# Revit family: 3_天吊埋込タイプ 排気消音タイプ 単相100V_3相200V-60
name_source: partatom
category: 機械設備
units: mm (PartAtom-declared; Revit-internal decimal feet)

## family parameters
OmniClass タイトル = Centrifugal Fans
OmniClass 番号 = 23.75.35.17.27
パーツ タイプ = 割り込み
ロード時にボイドで切り取り = いいえ
丸型コネクタ寸法 = 直径を使用
作業面ベース = いいえ
共有 = いいえ
常に垂直 = はい
部屋計算ポイント = はい

## types (6) — shared parameters
Clearance Left = 450  [stored 1.47638 ft]
Height = 350  [stored 1.14829 ft]
IfcExportAs = IfcFanType
IfcExportType = CENTRIFUGALFORWARDCURVED
MID静圧 = 0.0 Pa
MID風量 = 0.0 m³/h
OmniClassCode = 23-33 31 19 13 15
URL = https://www.mitsubishielectric.co.jp
Uniclass2015Code = Pr_65_67_29_12
Uniclass2015Title = Centrifugal fans
Uniclass2015Version = Systems v1.9
サービススペース = はい
ファンの種類 = 多翼形
仕様書バージョン = Version1.0
企業コード = 108420
分類コード = 50052502100020
周波数 = 60 Hz
呼称 = 消音ボックス付送風機
実風量 = 0.0 m³/h
本体マテリアル = 溶融亜鉛めっき鋼板
極 = 4
法定耐用年数 = 15
番手 = ♯1 1/2
盤工事区分 = 電気工事
積算_科目 = 2 換気設備
製品リリース年月 = 2008年12月1日
製品出荷対象 = 国内
製造元 = 三菱電機株式会社
設置方法 = 天吊
説明 = ストレートシロッコファン天吊埋込タイプ（消音形排気消音タイプ）
負荷分類 = 3_ファン類
運転質量 = 0.00 kg
zero-valued in all types: Clearance Back, Clearance Bottom, Clearance Front, Clearance Right, Clearance Top

## per-type parameters (varying)
| type | Depth | M | MAX静圧 | MAX風量 | MIN静圧 | MIN風量 | Width | ダクト径 | 価格 | 天吊金具ピッチ奥行 | 天吊金具ピッチ幅 | 形名 | 極数 | 消費電力 | 相 | 製品質量 | 質量 | 電動機出力 | 電圧 | 騒音レベル(dB(A)) | 騒音レベル(dB(A))_側面 | 騒音レベル(dB(A))_吐出 | 騒音レベル(dB(A))_吸込 |
| BFS-120SHU | 887  [stored 2.9101 ft] | 85  [stored 0.278871 ft] | 265.0 Pa | 1200.0 m³/h | 179.0 Pa | 989.0 m³/h | 455  [stored 1.49278 ft] | 250 mm | 179000 $ | 851  [stored 2.79199 ft] | 550  [stored 1.80446 ft] | BFS-SHU : BFS-120SHU | 2 | 330 W | 1 | 28.00 kg | 33.60 kg | 270 W | 100 V | 47 | 35 | 47 | 41.5 |
| BFS-150SHU | 1041 | 85  [stored 0.278871 ft] | 294.0 Pa | 1500.0 m³/h | 179.0 Pa | 1164.0 m³/h | 455  [stored 1.49278 ft] | 250 mm | 186000 $ | 1005  [stored 3.29724 ft] | 550  [stored 1.80446 ft] | BFS-SHU : BFS-150SHU | 2 | 480 W | 1 | 30.00 kg | 36.00 kg | 300 W | 100 V | 50 | 37 | 50 | 42.5 |
| BFS-120THU | 887  [stored 2.9101 ft] | 85  [stored 0.278871 ft] | 265.0 Pa | 1200.0 m³/h | 119.0 Pa | 789.0 m³/h | 455  [stored 1.49278 ft] | 250 mm | 179000 $ | 851  [stored 2.79199 ft] | 550  [stored 1.80446 ft] | BFS-THU : BFS-120THU | 3 | 330 W | 3 | 28.00 kg | 33.60 kg | 240 W | 200 V | 47 | 35 | 47 | 41.5 |
| BFS-150THU | 1041 | 85  [stored 0.278871 ft] | 294.0 Pa | 1500.0 m³/h | 129.0 Pa | 995.0 m³/h | 455  [stored 1.49278 ft] | 250 mm | 186000 $ | 1005  [stored 3.29724 ft] | 550  [stored 1.80446 ft] | BFS-THU : BFS-150THU | 3 | 455 W | 3 | 30.00 kg | 36.00 kg | 300 W | 200 V | 50 | 37 | 50 | 42.5 |
| BFS-180THU | 1041 | 85  [stored 0.278871 ft] | 314.0 Pa | 1800.0 m³/h | 0.0 Pa | 0.0 m³/h | 505  [stored 1.65682 ft] | 250 mm | 218000 $ | 1005  [stored 3.29724 ft] | 600 | BFS-THU : BFS-180THU | 3 | 565 W | 3 | 32.00 kg | 38.40 kg | 550 W | 200 V | 51 | 38 | 51 | 43.5 |
| BFS-210THU | 1178 | 100  [stored 0.328084 ft] | 322.0 Pa | 2100.0 m³/h | 0.0 Pa | 0.0 m³/h | 525 | 300 mm | 270000 $ | 1142  [stored 3.74672 ft] | 620  [stored 2.03412 ft] | BFS-THU : BFS-210THU | 3 | 680 W | 3 | 34.00 kg | 40.80 kg | 750 W | 200 V | 52 | 39.5 | 52 | 45 |

note: column(s) folded — value = type name in every type: モデル

note: [stored X ft] marks values corroborated as IEEE doubles in the binary element streams (Revit-internal decimal feet)
